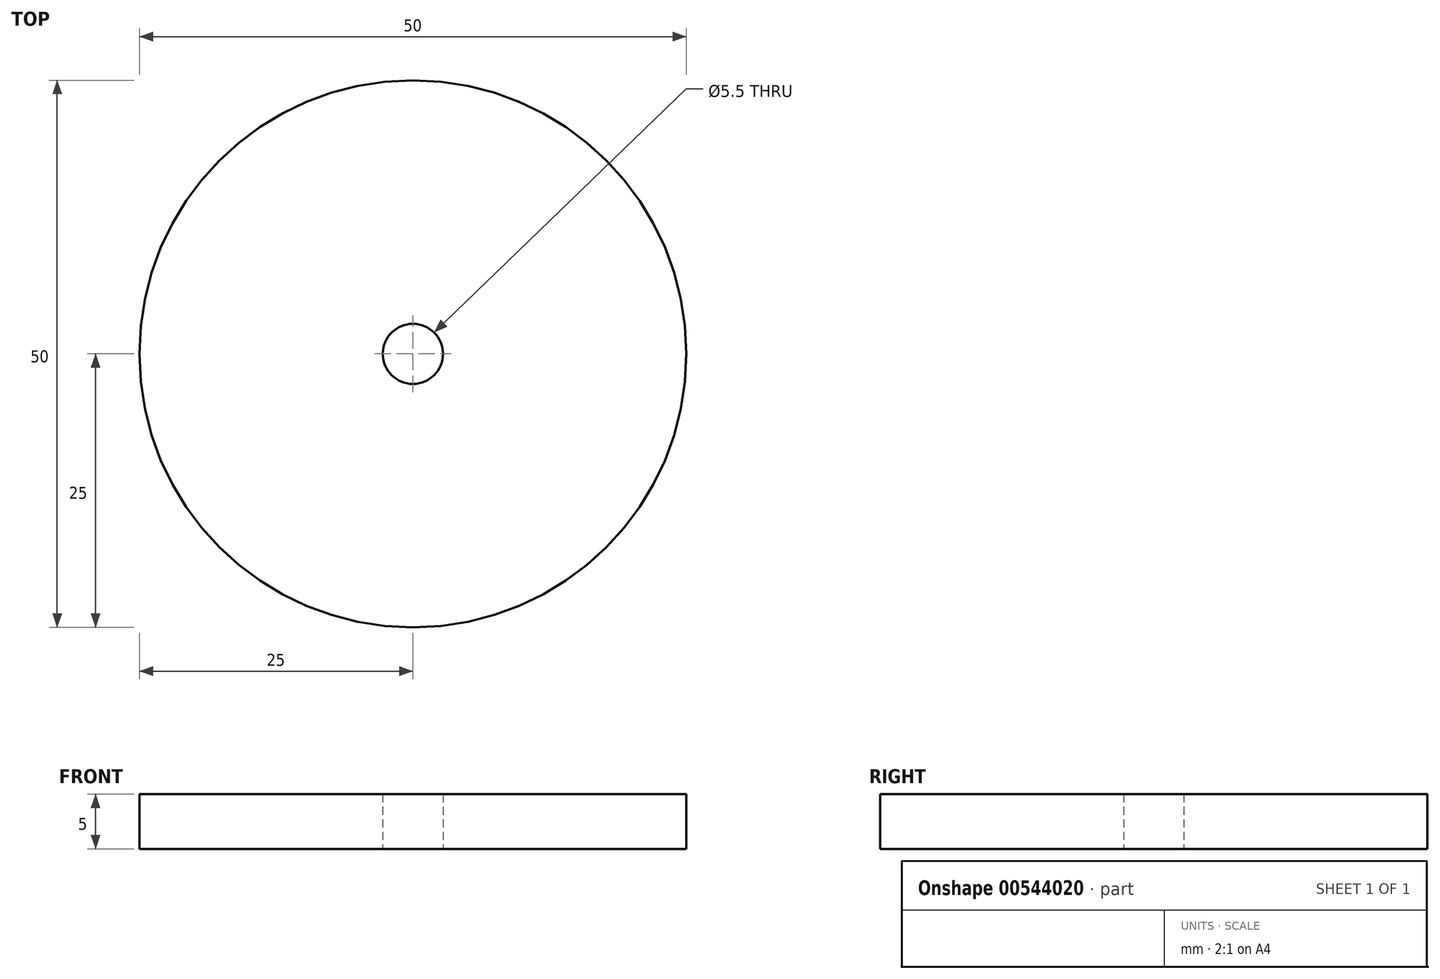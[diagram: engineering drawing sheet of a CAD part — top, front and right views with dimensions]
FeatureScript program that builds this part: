
annotation { "Feature Type Name" : "Feature", "Feature Type Description" : "" }
export const myFeature = defineFeature(function(context is Context, id is Id, definition is map)
    precondition{}
    {
        {
            var Q0;
            Q0=qCreatedBy(makeId("Top.planeOp"),FACE);
            var sketch = newSketch(context, id + "F0", { "sketchPlane" : qUnion([Q0])});
            skCircle(sketch, "E0", {"center": v(0, 0) * mm, "radius": 25 * mm});
            skCircle(sketch, "E1", {"center": v(0, 0) * mm, "radius": 2.75 * mm});
            skSolve(sketch);
        }
        {
            var Q0;
            Q0 = qSketchRegion(id + "F0", true);
            extrude(context, id + "F1", {"entities" : qUnion([Q0]), "depth" : 5 * mm, "offsetDistance" : 25 * mm});
        }
    });
